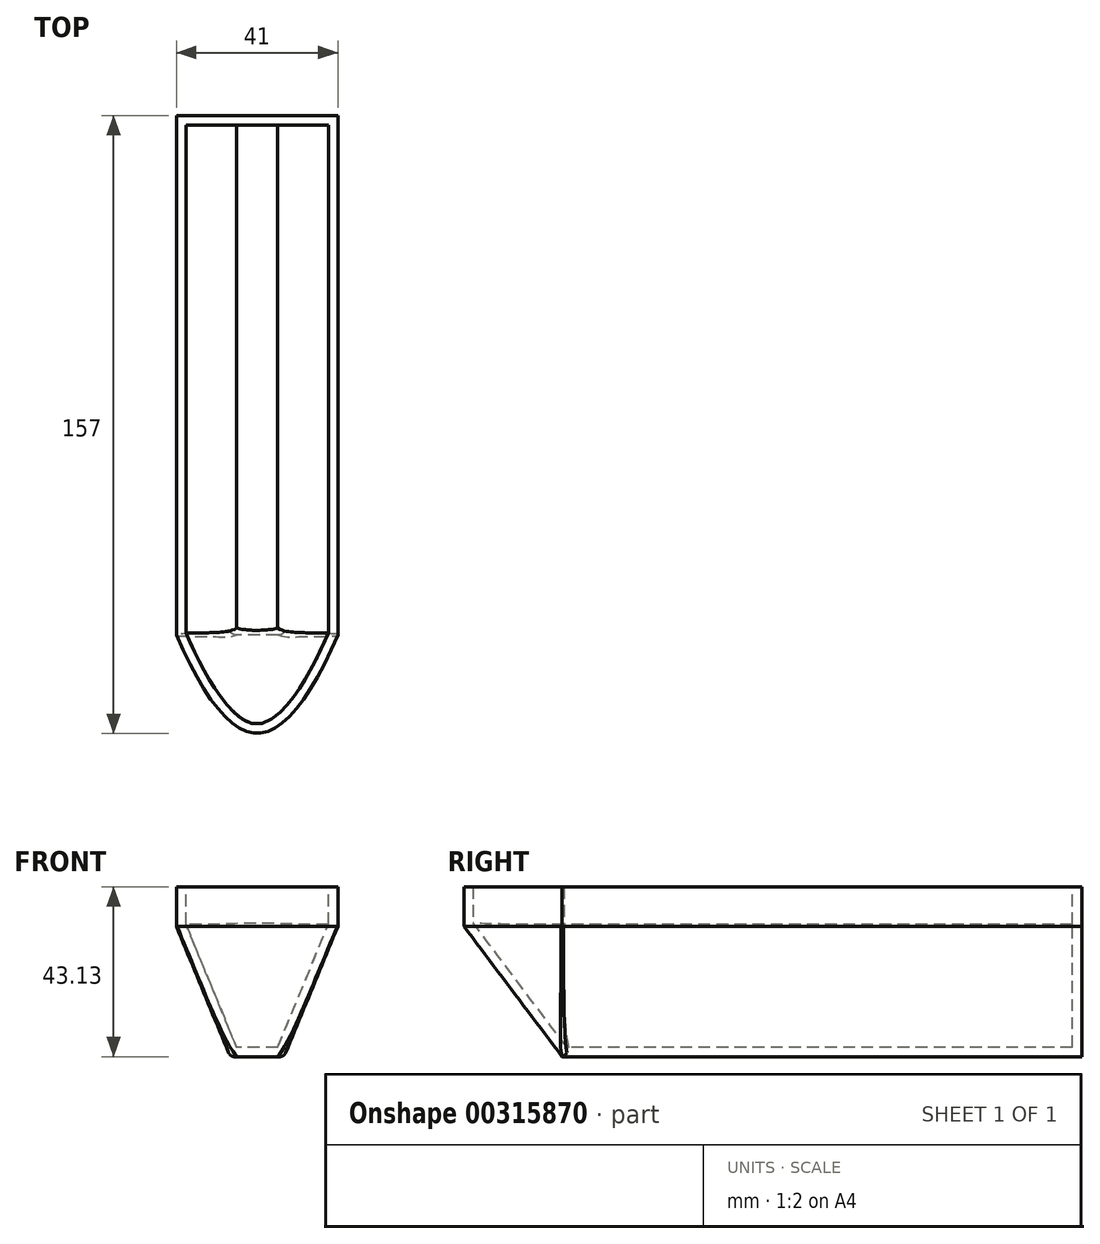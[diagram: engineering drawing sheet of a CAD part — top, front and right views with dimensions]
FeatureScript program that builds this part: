
annotation { "Feature Type Name" : "Feature", "Feature Type Description" : "" }
export const myFeature = defineFeature(function(context is Context, id is Id, definition is map)
    precondition{}
    {
        {
            var Q0;
            Q0=qCreatedBy(makeId("Top.planeOp"),FACE);
            cPlane(context, id + "F0", {"entities" : qUnion([Q0]), "cplaneType" : CPlaneType.OFFSET, "offset" : 33.12 * mm, "width" : 150 * mm, "height" : 150 * mm});
        }
        {
            var Q0;
            Q0=qCreatedBy(id+"F0.planeOp",FACE);
            var sketch = newSketch(context, id + "F1", { "sketchPlane" : qUnion([Q0])});
            skLineSegment(sketch, "E0", {"start": v(20.5, 132) * mm, "end": v(-20.5, 132) * mm});
            skLineSegment(sketch, "E1", {"start": v(20.5, 132) * mm, "end": v(20.5, 0) * mm});
            skLineSegment(sketch, "E2", {"start": v(-20.5, 132) * mm, "end": v(-20.5, 0) * mm});
            skPoint(sketch, "E3", {"position": v(0, -25) * mm});
            skFitSpline(sketch, "E4", {"points": [v(20.5, 0) * mm, v(0, -25) * mm, v(-20.5, 0) * mm], "startDerivative": vector(-39, -90) * mm, "endDerivative": vector(-39, 90) * mm});
            skSolve(sketch);
        }
        {
            var Q0;
            Q0=qCreatedBy(makeId("Top.planeOp"),FACE);
            var sketch = newSketch(context, id + "F2", { "sketchPlane" : qUnion([Q0])});
            skPoint(sketch, "E5", {"position": v(0, 0) * mm});
            skLineSegment(sketch, "E6", {"start": v(-6.83, 132) * mm, "end": v(6.83, 132) * mm});
            skLineSegment(sketch, "E7", {"start": v(6.83, 132) * mm, "end": v(6.83, 0) * mm});
            skLineSegment(sketch, "E8", {"start": v(6.83, 0) * mm, "end": v(-6.83, 0) * mm});
            skLineSegment(sketch, "E9", {"start": v(-6.83, 0) * mm, "end": v(-6.83, 132) * mm});
            skSolve(sketch);
        }
        {
            var Q0;
            Q0=makeQuery(id+"F1.imprint","IMPRINT",FACE,{"disambiguationData":[TD([[makeQuery(id+"F1.imprint","IMPRINT",EDGE,{"derivedFrom":sQuery(id+"F1.wireOp",EDGE,"E0")}),1.0]])]});
            var Q1;
            Q1=makeQuery(id+"F2.imprint","IMPRINT",FACE,{"disambiguationData":[TD([[makeQuery(id+"F2.imprint","IMPRINT",EDGE,{"derivedFrom":sQuery(id+"F2.wireOp",EDGE,"E6")}),-1.0]])]});
            loft(context, id + "F3", {"sheetProfilesArray" : [{ "sheetProfileEntities" : qUnion([Q0]) }, { "sheetProfileEntities" : qUnion([Q1]) }]});
        }
        {
            var Q0;
            Q0=makeQuery(id+"F1.imprint","IMPRINT",FACE,{"disambiguationData":[TD([[makeQuery(id+"F1.imprint","IMPRINT",EDGE,{"derivedFrom":sQuery(id+"F1.wireOp",EDGE,"E0")}),1.0]])]});
            extrude(context, id + "F4", {"entities" : qUnion([Q0]), "operationType" : NewBodyOperationType.ADD, "depth" : 10 * mm});
        }
        {
            var Q0;
            Q0=makeQuery(id+"F4.opExtrude","CAP_FACE",FACE,{"disambiguationData":[OSD([sQuery(id+"F1.wireOp",EDGE,"E0"),sQuery(id+"F1.wireOp",EDGE,"E1"),sQuery(id+"F1.wireOp",EDGE,"E2"),sQuery(id+"F1.wireOp",EDGE,"E4")])],"isStart":false});
            shell(context, id + "F5", {"entities" : qUnion([Q0]), "thickness" : 2.4 * mm});
        }
        {
            var Q0;
            Q0=makeQuery(id+"F3.opLoft","MID_CAP_EDGE",EDGE,{"disambiguationData":[OSD([sQuery(id+"F2.wireOp",EDGE,"E6"),sQuery(id+"F2.wireOp",EDGE,"E8"),sQuery(id+"F2.wireOp",EDGE,"E9")])],"capPos":1.0});
            var Q1;
            Q1=makeQuery(id+"F3.opLoft","MID_CAP_EDGE",EDGE,{"disambiguationData":[OSD([sQuery(id+"F2.wireOp",EDGE,"E6"),sQuery(id+"F2.wireOp",EDGE,"E7"),sQuery(id+"F2.wireOp",EDGE,"E8")])],"capPos":1.0});
            var Q2;
            Q2=makeQuery(id+"F3.opLoft","SWEPT_EDGE",EDGE,{"disambiguationData":[OSD([sQuery(id+"F1.wireOp",EDGE,"E1"),sQuery(id+"F1.wireOp",EDGE,"E4"),sQuery(id+"F2.wireOp",EDGE,"E7"),sQuery(id+"F2.wireOp",EDGE,"E8")])]});
            var Q3;
            Q3=makeQuery(id+"F3.opLoft","SWEPT_EDGE",EDGE,{"disambiguationData":[OSD([sQuery(id+"F1.wireOp",EDGE,"E2"),sQuery(id+"F1.wireOp",EDGE,"E4"),sQuery(id+"F2.wireOp",EDGE,"E8"),sQuery(id+"F2.wireOp",EDGE,"E9")])]});
            fillet(context, id + "F6", {"entities" : qUnion([Q0, Q1, Q2, Q3]), "radius" : 1.6 * mm, "tangentPropagation" : true, "allowEdgeOverflow" : false});
        }
    });
